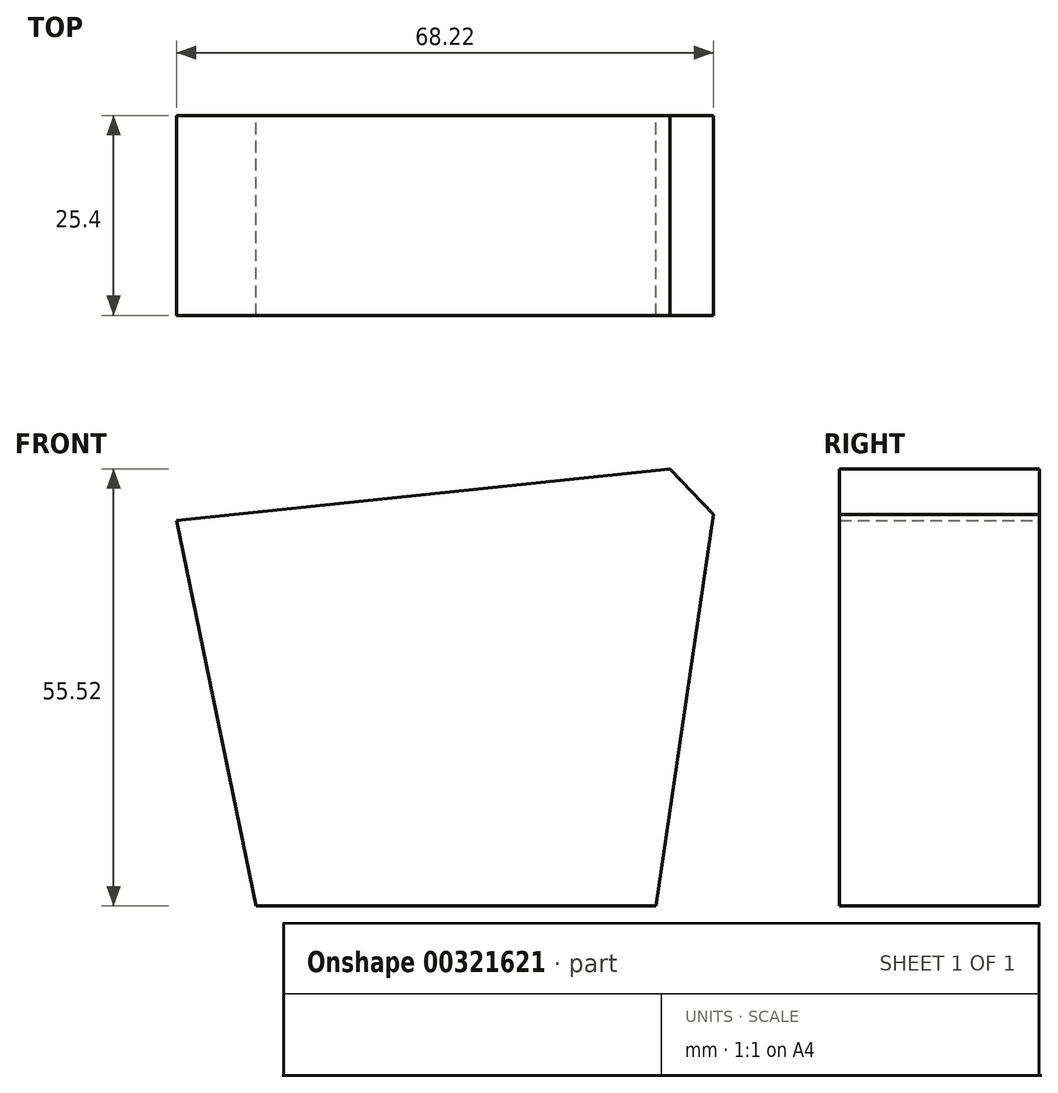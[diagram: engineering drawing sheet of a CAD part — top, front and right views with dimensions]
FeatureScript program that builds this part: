
annotation { "Feature Type Name" : "Feature", "Feature Type Description" : "" }
export const myFeature = defineFeature(function(context is Context, id is Id, definition is map)
    precondition{}
    {
        {
            var Q0;
            Q0=qCreatedBy(makeId("Front.planeOp"),FACE);
            var sketch = newSketch(context, id + "F0", { "sketchPlane" : qUnion([Q0])});
            skLineSegment(sketch, "E0", {"start": v(-39.63, 19.1) * mm, "end": v(-29.54, -29.9) * mm});
            skLineSegment(sketch, "E1", {"start": v(-29.54, -29.9) * mm, "end": v(21.26, -29.9) * mm});
            skLineSegment(sketch, "E2", {"start": v(21.26, -29.9) * mm, "end": v(29.54, 26.3) * mm});
            skLineSegment(sketch, "E3", {"start": v(29.54, 26.3) * mm, "end": v(-39.63, 19.1) * mm});
            skSolve(sketch);
        }
        {
            var Q0;
            Q0 = qSketchRegion(id + "F0", true);
            var Q1;
            Q1=makeQuery(id+"F0.imprint","IMPRINT",FACE,{"disambiguationData":[TD([[makeQuery(id+"F0.imprint","IMPRINT",EDGE,{"derivedFrom":sQuery(id+"F0.wireOp",EDGE,"E0")}),1.0]])]});
            extrude(context, id + "F1", {"entities" : qUnion([Q0, Q1]), "depth" : 25.4 * mm});
        }
        {
            var Q0;
            Q0=makeQuery(id+"F1.opExtrude","SWEPT_EDGE",EDGE,{"disambiguationData":[OSD([sQuery(id+"F0.wireOp",EDGE,"E2"),sQuery(id+"F0.wireOp",EDGE,"E3")])]});
            chamfer(context, id + "F2", {"entities" : qUnion([Q0]), "width" : 5.08 * mm, "tangentPropagation" : true});
        }
    });
